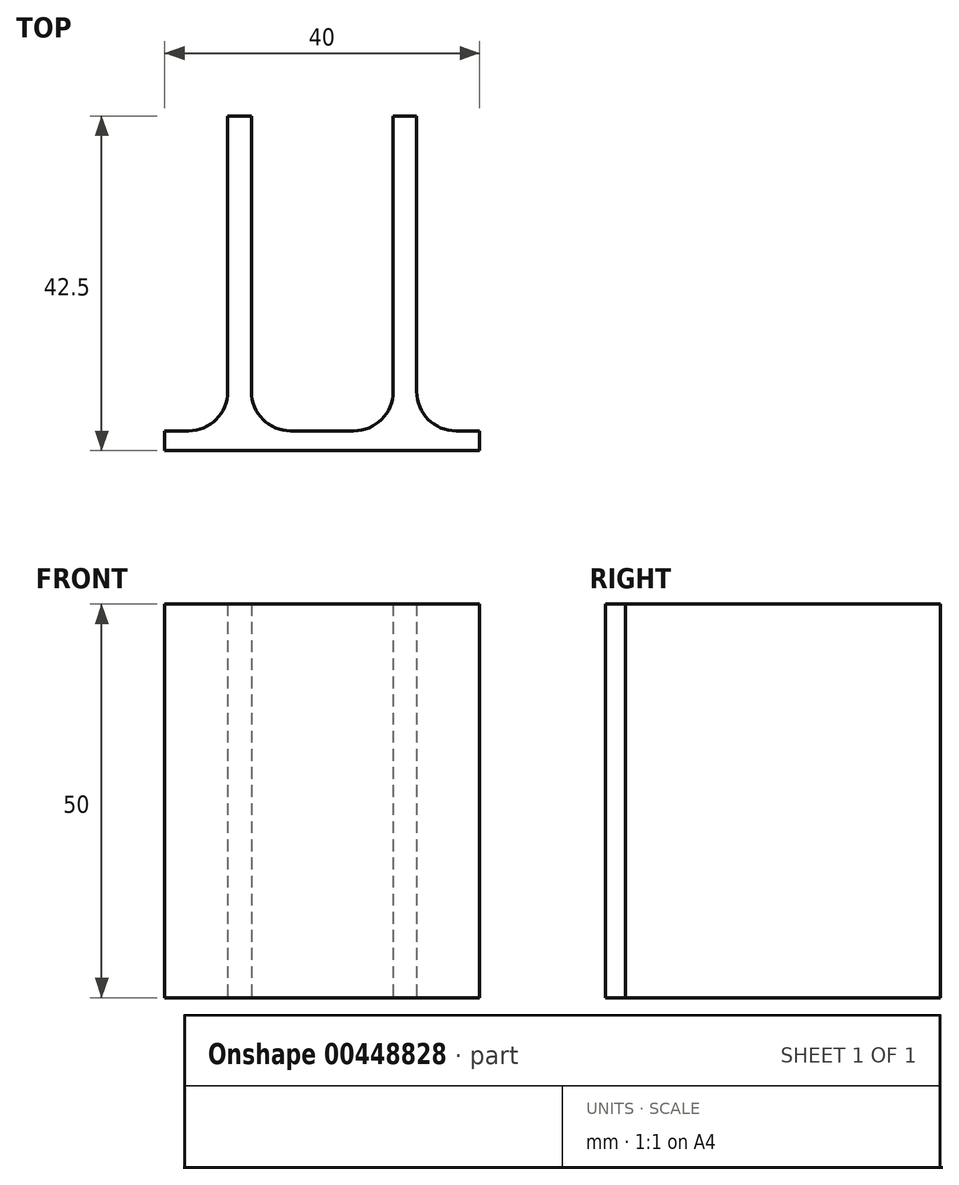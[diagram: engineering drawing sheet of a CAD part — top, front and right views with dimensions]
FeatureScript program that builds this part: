
annotation { "Feature Type Name" : "Feature", "Feature Type Description" : "" }
export const myFeature = defineFeature(function(context is Context, id is Id, definition is map)
    precondition{}
    {
        {
            var Q0;
            Q0=qCreatedBy(makeId("Top.planeOp"),FACE);
            var sketch = newSketch(context, id + "F0", { "sketchPlane" : qUnion([Q0])});
            skLineSegment(sketch, "E0.bottom", {"start": v(-20, -1.25) * mm, "end": v(20, -1.25) * mm});
            skLineSegment(sketch, "E0.top", {"start": v(-20, 1.25) * mm, "end": v(20, 1.25) * mm});
            skLineSegment(sketch, "E0.left", {"start": v(-20, -1.25) * mm, "end": v(-20, 1.25) * mm});
            skLineSegment(sketch, "E0.right", {"start": v(20, -1.25) * mm, "end": v(20, 1.25) * mm});
            skPoint(sketch, "E0.middle", {"position": v(0, 0) * mm});
            skLineSegment(sketch, "E1.bottom", {"start": v(12, 41.25) * mm, "end": v(-12, 41.25) * mm});
            skLineSegment(sketch, "E1.top", {"start": v(12, -38.75) * mm, "end": v(-12, -38.75) * mm});
            skLineSegment(sketch, "E1.left", {"start": v(12, 41.25) * mm, "end": v(12, -38.75) * mm});
            skLineSegment(sketch, "E1.right", {"start": v(-12, 41.25) * mm, "end": v(-12, -38.75) * mm});
            skPoint(sketch, "E1.middle", {"position": v(0, 1.25) * mm});
            skLineSegment(sketch, "E2.bottom", {"start": v(9, 1.25) * mm, "end": v(-9, 1.25) * mm});
            skLineSegment(sketch, "E2.top", {"start": v(9, 81.25) * mm, "end": v(-9, 81.25) * mm});
            skLineSegment(sketch, "E2.left", {"start": v(9, 1.25) * mm, "end": v(9, 81.25) * mm});
            skLineSegment(sketch, "E2.right", {"start": v(-9, 1.25) * mm, "end": v(-9, 81.25) * mm});
            skPoint(sketch, "E2.middle", {"position": v(0, 41.25) * mm});
            skSolve(sketch);
        }
        {
            var Q0;
            {var subQ0=sQuery(id+"F0.wireOp",EDGE,"E0.right");Q0=makeQuery(id+"F0.imprint","IMPRINT",FACE,{"disambiguationData":[TD([[makeQuery(id+"F0.imprint","IMPRINT",EDGE,{"derivedFrom":subQ0}),1.0]])]});}
            var Q1;
            {var subQ0=sQuery(id+"F0.wireOp",EDGE,"E1.right");var subQ1=sQuery(id+"F0.wireOp",EDGE,"E0.bottom");var subQ2=makeQuery(id+"F0.imprint","INTERSECT",VERTEX,{"derivedFrom":[subQ1,subQ0]});Q1=makeQuery(id+"F0.imprint","IMPRINT",FACE,{"disambiguationData":[TD([[makeQuery(id+"F0.imprint","IMPRINT",EDGE,{"disambiguationData":[TD([[subQ2,-1.0]])],"derivedFrom":subQ1}),1.0]])]});}
            var Q2;
            {var subQ3=sQuery(id+"F0.wireOp",EDGE,"E0.left");Q2=makeQuery(id+"F0.imprint","IMPRINT",FACE,{"disambiguationData":[TD([[makeQuery(id+"F0.imprint","IMPRINT",EDGE,{"derivedFrom":subQ3}),-1.0]])]});}
            var Q3;
            {var subQ0=sQuery(id+"F0.wireOp",EDGE,"E2.left");var subQ1=sQuery(id+"F0.wireOp",EDGE,"E0.top");var subQ2=makeQuery(id+"F0.imprint","INTERSECT",VERTEX,{"derivedFrom":[subQ1,subQ0]});Q3=makeQuery(id+"F0.imprint","IMPRINT",FACE,{"disambiguationData":[TD([[makeQuery(id+"F0.imprint","IMPRINT",EDGE,{"disambiguationData":[TD([[subQ2,-1.0]])],"derivedFrom":subQ1}),1.0]])]});}
            var Q4;
            {var subQ0=sQuery(id+"F0.wireOp",EDGE,"E2.right");var subQ1=sQuery(id+"F0.wireOp",EDGE,"E0.top");var subQ2=makeQuery(id+"F0.imprint","INTERSECT",VERTEX,{"derivedFrom":[subQ1,subQ0]});Q4=makeQuery(id+"F0.imprint","IMPRINT",FACE,{"disambiguationData":[TD([[makeQuery(id+"F0.imprint","IMPRINT",EDGE,{"disambiguationData":[TD([[subQ2,1.0]])],"derivedFrom":subQ1}),1.0]])]});}
            extrude(context, id + "F1", {"entities" : qUnion([Q0, Q1, Q2, Q3, Q4]), "depth" : 50 * mm, "offsetDistance" : 25 * mm});
        }
        {
            var Q0;
            Q0=makeQuery(id+"F1.opExtrude","SWEPT_EDGE",EDGE,{"disambiguationData":[OSD([sQuery(id+"F0.wireOp",EDGE,"E0.top"),sQuery(id+"F0.wireOp",EDGE,"E1.left")])]});
            var Q1;
            Q1=makeQuery(id+"F1.opExtrude","SWEPT_EDGE",EDGE,{"disambiguationData":[OSD([sQuery(id+"F0.wireOp",EDGE,"E0.top"),sQuery(id+"F0.wireOp",EDGE,"E1.right")])]});
            var Q2;
            Q2=makeQuery(id+"F1.opExtrude","SWEPT_EDGE",EDGE,{"disambiguationData":[OSD([sQuery(id+"F0.wireOp",EDGE,"E0.top"),sQuery(id+"F0.wireOp",EDGE,"E2.right")])]});
            var Q3;
            Q3=makeQuery(id+"F1.opExtrude","SWEPT_EDGE",EDGE,{"disambiguationData":[OSD([sQuery(id+"F0.wireOp",EDGE,"E0.top"),sQuery(id+"F0.wireOp",EDGE,"E2.left")])]});
            fillet(context, id + "F2", {"entities" : qUnion([Q0, Q1, Q2, Q3]), "tangentPropagation" : true, "radius" : 5 * mm, "defaultsChanged" : false, "vertexSettings" : [], "allowEdgeOverflow" : false});
        }
    });
